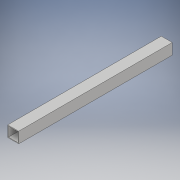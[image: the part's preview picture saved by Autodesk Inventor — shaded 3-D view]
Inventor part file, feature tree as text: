
AUTODESK INVENTOR PART (.ipt)
format: ipt  version: 2019 (Build 230136000, 136)  size: 97,280 bytes
history: native  units: in
note: dims shown in document units (in); Inventor stores cm internally (conversion verified against a paired STEP export)
features: extrude x1, sketch x1
ambient origin geometry x8: Origin, YZ Plane, XZ Plane, XY Plane, X Axis, Y Axis, Z Axis, Center Point
bodies: Solid1 (feature_tree)
feature tree (2):
  extrude  "Extrusion1"  Depth=2.0in
  sketch  "Sketch1"  dims[d0=2.0in d1=2.0in d2=0.125in d3=28.0in d4=0.0in]
